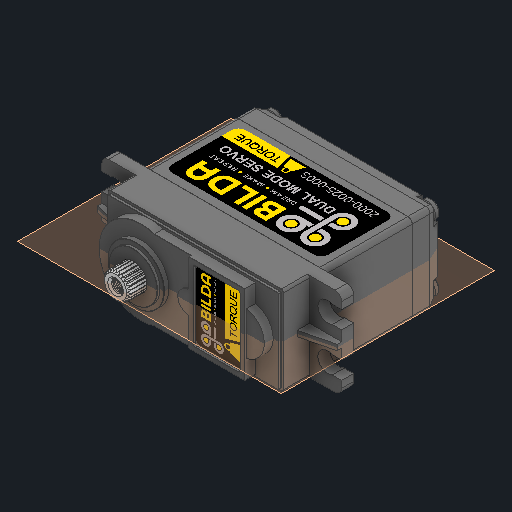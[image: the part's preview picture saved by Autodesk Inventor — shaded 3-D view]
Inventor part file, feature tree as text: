
AUTODESK INVENTOR PART (.ipt)
format: ipt  version: 2023 (Build 270158000, 158)  size: 2,011,648 bytes
history: native  units: in
note: dims shown in document units (in); Inventor stores cm internally (conversion verified against a paired STEP export)
features: other x6, sketch x2
ambient origin geometry x8: Origin, YZ Plane, XZ Plane, XY Plane, X Axis, Y Axis, Z Axis, Center Point
bodies: Solid1 (feature_tree), Solid2 (feature_tree)
feature tree (8):
  parser-record x1  (decoder bookkeeping rows leaked as tree rows — omitted from the tree; the rows remain in map.json)
  sketch  "Sketch1"
  sketch  "Sketch2"
  other  "Decal1"
  other  "Decal2"
  other  "Image3"
  other  "Image4"
  other  "Join1[1]"
